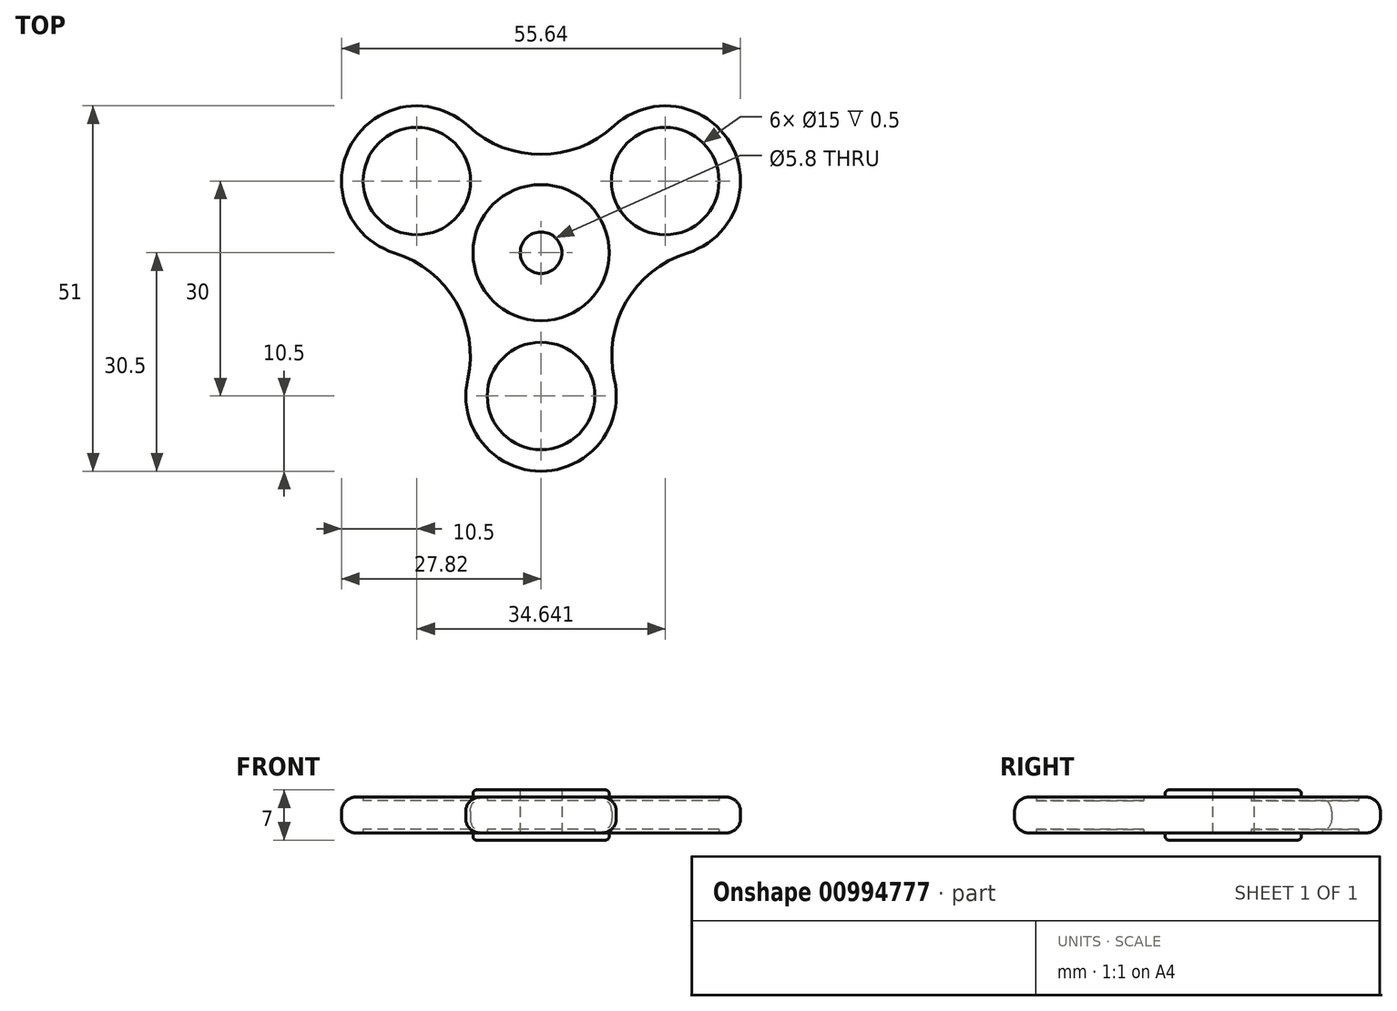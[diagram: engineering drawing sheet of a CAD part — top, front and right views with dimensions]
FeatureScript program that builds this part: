
annotation { "Feature Type Name" : "Feature", "Feature Type Description" : "" }
export const myFeature = defineFeature(function(context is Context, id is Id, definition is map)
    precondition{}
    {
        {
            var Q0;
            Q0=qCreatedBy(makeId("Top.planeOp"),FACE);
            var sketch = newSketch(context, id + "F0", { "sketchPlane" : qUnion([Q0])});
            skCircle(sketch, "E0", {"center": v(0, 0) * mm, "radius": 7.5 * mm});
            skCircle(sketch, "E1", {"center": v(0, -20) * mm, "radius": 7.5 * mm});
            skArc(sketch, "E2", {"start": v(-10.24, -17.68) * mm, "mid": v(0, -30.5) * mm, "end": v(10.24, -17.68) * mm});
            skArc(sketch, "E3.1.0", {"start": v(20.43, -0.03) * mm, "mid": v(26.41, 15.25) * mm, "end": v(10.19, 17.7) * mm});
            skCircle(sketch, "E3.1.1", {"center": v(17.32, 10) * mm, "radius": 7.5 * mm});
            skArc(sketch, "E3.2.0", {"start": v(-10.19, 17.7) * mm, "mid": v(-26.41, 15.25) * mm, "end": v(-20.43, -0.03) * mm});
            skCircle(sketch, "E3.2.1", {"center": v(-17.32, 10) * mm, "radius": 7.5 * mm});
            skArc(sketch, "E4", {"start": v(-10.24, -17.68) * mm, "mid": v(-11.88, -6.86) * mm, "end": v(-20.43, -0.03) * mm});
            skArc(sketch, "E5.1.0", {"start": v(20.43, -0.03) * mm, "mid": v(11.88, -6.86) * mm, "end": v(10.24, -17.68) * mm});
            skArc(sketch, "E5.2.0", {"start": v(-10.19, 17.7) * mm, "mid": v(0, 13.71) * mm, "end": v(10.19, 17.7) * mm});
            skSolve(sketch);
        }
        {
            var Q0;
            Q0=makeQuery(id+"F0.imprint","IMPRINT",FACE,{"disambiguationData":[TD([[makeQuery(id+"F0.imprint","IMPRINT",EDGE,{"derivedFrom":sQuery(id+"F0.wireOp",EDGE,"E0")}),-1.0]])]});
            extrude(context, id + "F1", {"entities" : qUnion([Q0]), "endBound" : BoundingType.SYMMETRIC, "depth" : 5 * mm, "offsetDistance" : 25 * mm});
        }
        {
            var Q0;
            Q0=makeQuery(id+"F0.imprint","IMPRINT",FACE,{"disambiguationData":[TD([[makeQuery(id+"F0.imprint","IMPRINT",EDGE,{"derivedFrom":sQuery(id+"F0.wireOp",EDGE,"E3.2.1")}),1.0]])]});
            var Q1;
            Q1=makeQuery(id+"F0.imprint","IMPRINT",FACE,{"disambiguationData":[TD([[makeQuery(id+"F0.imprint","IMPRINT",EDGE,{"derivedFrom":sQuery(id+"F0.wireOp",EDGE,"E1")}),1.0]])]});
            var Q2;
            Q2=makeQuery(id+"F0.imprint","IMPRINT",FACE,{"disambiguationData":[TD([[makeQuery(id+"F0.imprint","IMPRINT",EDGE,{"derivedFrom":sQuery(id+"F0.wireOp",EDGE,"E3.1.1")}),1.0]])]});
            extrude(context, id + "F2", {"entities" : qUnion([Q0, Q1, Q2]), "operationType" : NewBodyOperationType.ADD, "endBound" : BoundingType.SYMMETRIC, "depth" : 4 * mm, "offsetDistance" : 25 * mm});
        }
        {
            var Q0;
            Q0=makeQuery(id+"F1.opExtrude","CAP_FACE",FACE,{"disambiguationData":[OSD([sQuery(id+"F0.wireOp",EDGE,"E0"),sQuery(id+"F0.wireOp",EDGE,"E1"),sQuery(id+"F0.wireOp",EDGE,"E2"),sQuery(id+"F0.wireOp",EDGE,"E3.1.0"),sQuery(id+"F0.wireOp",EDGE,"E3.1.1"),sQuery(id+"F0.wireOp",EDGE,"E3.2.0"),sQuery(id+"F0.wireOp",EDGE,"E3.2.1"),sQuery(id+"F0.wireOp",EDGE,"E4"),sQuery(id+"F0.wireOp",EDGE,"E5.1.0"),sQuery(id+"F0.wireOp",EDGE,"E5.2.0")])],"isStart":false});
            var sketch = newSketch(context, id + "F3", { "sketchPlane" : qUnion([Q0])});
            skCircle(sketch, "E6.0", {"center": v(0, 0) * mm, "radius": 7 * mm});
            skCircle(sketch, "E7", {"center": v(0, 0) * mm, "radius": 3 * mm});
            skCircle(sketch, "E8.0", {"center": v(0, 0) * mm, "radius": 9.5 * mm});
            skSolve(sketch);
        }
        {
            var Q0;
            Q0=makeQuery(id+"F3.imprint","IMPRINT",FACE,{"disambiguationData":[TD([[makeQuery(id+"F3.imprint","IMPRINT",EDGE,{"derivedFrom":sQuery(id+"F3.wireOp",EDGE,"E6.0")}),1.0]])]});
            extrude(context, id + "F4", {"entities" : qUnion([Q0]), "oppositeDirection" : true, "depth" : 5.1 * mm, "offsetDistance" : 25 * mm});
        }
        {
            var Q0;
            Q0=makeQuery(id+"F3.imprint","IMPRINT",FACE,{"disambiguationData":[TD([[makeQuery(id+"F3.imprint","IMPRINT",EDGE,{"derivedFrom":sQuery(id+"F3.wireOp",EDGE,"E8.0")}),1.0]])]});
            var Q1;
            Q1=makeQuery(id+"F3.imprint","IMPRINT",FACE,{"disambiguationData":[TD([[makeQuery(id+"F3.imprint","IMPRINT",EDGE,{"derivedFrom":sQuery(id+"F3.wireOp",EDGE,"E6.0")}),-1.0]])]});
            var Q2;
            Q2=makeQuery(id+"F3.imprint","IMPRINT",FACE,{"disambiguationData":[TD([[makeQuery(id+"F3.imprint","IMPRINT",EDGE,{"derivedFrom":sQuery(id+"F3.wireOp",EDGE,"E6.0")}),1.0]])]});
            extrude(context, id + "F5", {"entities" : qUnion([Q0, Q1, Q2]), "operationType" : NewBodyOperationType.ADD, "depth" : 1 * mm, "offsetDistance" : 25 * mm});
        }
        {
            var Q0;
            Q0=makeQuery(id+"F1.opExtrude","CAP_FACE",FACE,{"disambiguationData":[OSD([sQuery(id+"F0.wireOp",EDGE,"E0"),sQuery(id+"F0.wireOp",EDGE,"E1"),sQuery(id+"F0.wireOp",EDGE,"E2"),sQuery(id+"F0.wireOp",EDGE,"E3.1.0"),sQuery(id+"F0.wireOp",EDGE,"E3.1.1"),sQuery(id+"F0.wireOp",EDGE,"E3.2.0"),sQuery(id+"F0.wireOp",EDGE,"E3.2.1"),sQuery(id+"F0.wireOp",EDGE,"E4"),sQuery(id+"F0.wireOp",EDGE,"E5.1.0"),sQuery(id+"F0.wireOp",EDGE,"E5.2.0")])],"isStart":true});
            var sketch = newSketch(context, id + "F6", { "sketchPlane" : qUnion([Q0])});
            skCircle(sketch, "E9.0", {"center": v(0, 0) * mm, "radius": 2.9 * mm});
            skCircle(sketch, "E10.0", {"center": v(0, 0) * mm, "radius": 9.5 * mm});
            skSolve(sketch);
        }
        {
            var Q0;
            Q0=makeQuery(id+"F6.imprint","IMPRINT",FACE,{"disambiguationData":[TD([[makeQuery(id+"F6.imprint","IMPRINT",EDGE,{"derivedFrom":sQuery(id+"F6.wireOp",EDGE,"E9.0")}),-1.0]])]});
            var Q1;
            Q1=makeQuery(id+"F5.opExtrude","CAP_FACE",FACE,{"disambiguationData":[OSD([sQuery(id+"F3.wireOp",EDGE,"E7"),sQuery(id+"F3.wireOp",EDGE,"E8.0")])],"isStart":false});
            extrude(context, id + "F7", {"entities" : qUnion([Q0]), "endBound" : BoundingType.UP_TO_SURFACE, "oppositeDirection" : true, "depth" : 25 * mm, "endBoundEntityFace" : qUnion([Q1]), "offsetDistance" : 25 * mm});
        }
        {
            var Q0;
            Q0 = qSketchRegion(id + "F6", true);
            var Q1;
            Q1=makeQuery(id+"F6.imprint","IMPRINT",FACE,{"disambiguationData":[TD([[makeQuery(id+"F6.imprint","IMPRINT",EDGE,{"derivedFrom":sQuery(id+"F6.wireOp",EDGE,"E9.0")}),-1.0]])]});
            extrude(context, id + "F8", {"entities" : qUnion([Q0, Q1]), "operationType" : NewBodyOperationType.ADD, "depth" : 1 * mm, "offsetDistance" : 25 * mm});
        }
        {
            var Q0;
            Q0=makeQuery(id+"F1.opExtrude","CAP_EDGE",EDGE,{"disambiguationData":[OSD([sQuery(id+"F0.wireOp",EDGE,"E2")])],"isStart":false});
            var Q1;
            Q1=makeQuery(id+"F1.opExtrude","CAP_EDGE",EDGE,{"disambiguationData":[OSD([sQuery(id+"F0.wireOp",EDGE,"E2")])],"isStart":true});
            fillet(context, id + "F9", {"entities" : qUnion([Q0, Q1]), "radius" : 2 * mm, "tangentPropagation" : true, "allowEdgeOverflow" : false});
        }
        {
            var Q0;
            Q0=makeQuery(id+"F8.opExtrude","CAP_EDGE",EDGE,{"disambiguationData":[OSD([sQuery(id+"F6.wireOp",EDGE,"E10.0")])],"isStart":false});
            var Q1;
            Q1=makeQuery(id+"F5.opExtrude","CAP_EDGE",EDGE,{"disambiguationData":[OSD([sQuery(id+"F3.wireOp",EDGE,"E8.0")])],"isStart":false});
            fillet(context, id + "F10", {"entities" : qUnion([Q0, Q1]), "radius" : 0.5 * mm, "tangentPropagation" : true, "allowEdgeOverflow" : false});
        }
    });
